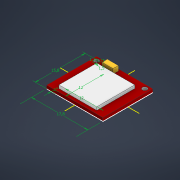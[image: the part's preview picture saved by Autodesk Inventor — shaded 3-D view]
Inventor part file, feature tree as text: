
AUTODESK INVENTOR PART (.ipt)
format: ipt  version: 2021 (Build 250183000, 183)  size: 137,728 bytes
history: native  units: mm
features: extrude x4, sketch x2, other x1
ambient origin geometry x8: Origin, YZ Plane, XZ Plane, XY Plane, X Axis, Y Axis, Z Axis, Center Point
bodies: Volumenkörper1 (feature_tree)
feature tree (7):
  other  "GSMModul"
  sketch  "Skizze1"  dims[d0=17.8mm d1=15.8mm]
  extrude  "Extrusion1"  Depth=15.8mm
  extrude  "Extrusion2"  Depth=12.0mm
  extrude  "Extrusion3"  Depth=1.0mm
  extrude  "Extrusion4"  Depth=1.0mm TaperAngle=0.0deg
  sketch  "Skizze2"  dims[d3=12.0mm d4=12.0mm d5=1.0mm d6=1.0mm d7=0.0mm d8=2.0mm d9=0.0mm d10=3.5mm d11=1.7mm d12=0.5mm d13=1.5mm d14=0.0mm d15=1.5mm d16=1.25mm d17=1.25mm d18=1.0mm d19=0.0mm]
